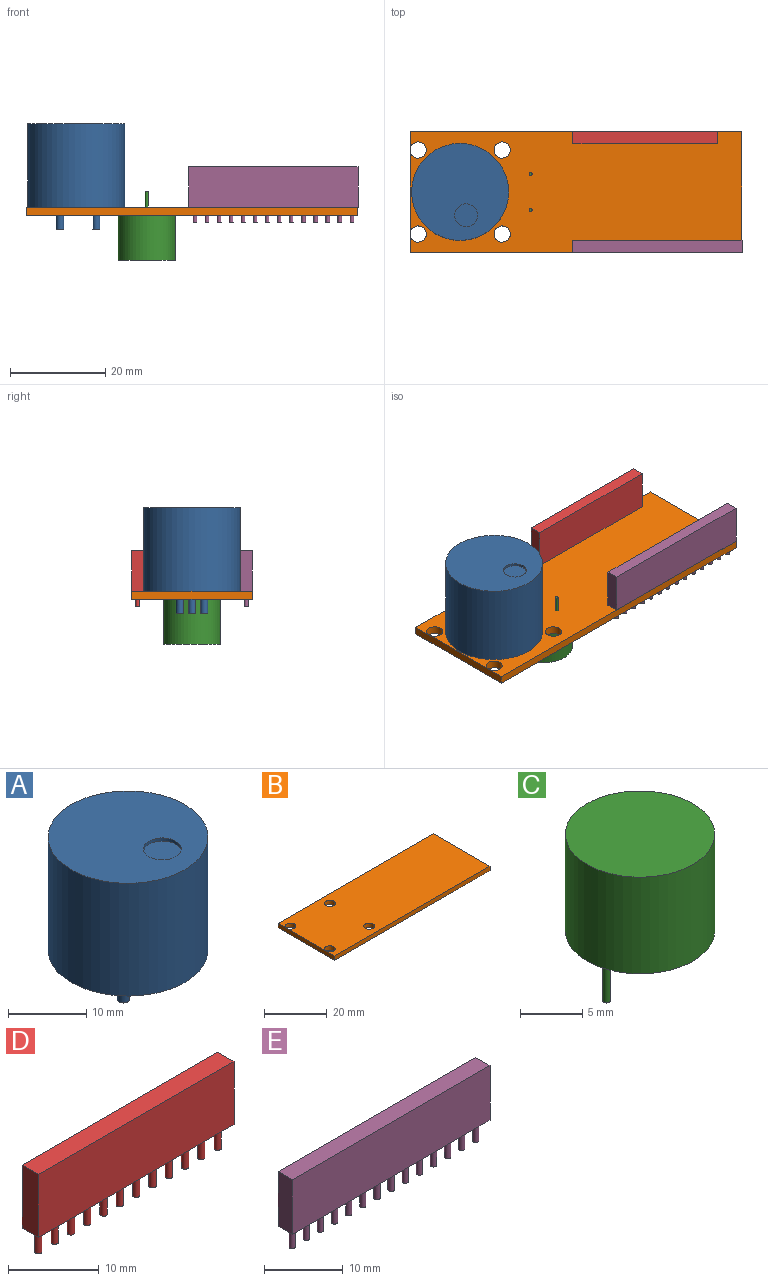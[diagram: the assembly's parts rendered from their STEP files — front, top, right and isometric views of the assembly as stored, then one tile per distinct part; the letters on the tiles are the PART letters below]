
ASSEMBLY  parts=5 mates=4
PART A: 11 faces, bbox 20.4x20.4x22.4 mm
  f0: cylinder r=10.2mm len=20.4mm, axis (0,0,-1), area 1128mm2, adj f1,f2
  f1: plane 20.4x20.4mm, normal (0,0,1), area 308.5mm2, adj f0,f9
  f2: plane 20.4x20.4mm, normal (0,0,-1), area 321mm2, adj f0,f3,f5,f7
  f3: cylinder r=0.79mm len=4.78mm, axis (0,0,1), area 23.6mm2, adj f2,f4
  f4: plane 1.57x1.57mm, normal (0,0,-1), area 1.9mm2, adj f3
  f5: cylinder r=0.79mm len=4.78mm, axis (0,0,1), area 23.6mm2, adj f2,f6
  f6: plane 1.57x1.57mm, normal (0,0,-1), area 1.9mm2, adj f5
  f7: cylinder r=0.79mm len=4.78mm, axis (0,0,1), area 23.6mm2, adj f2,f8
  f8: plane 1.57x1.57mm, normal (0,0,-1), area 1.9mm2, adj f7
  f9: cylinder r=2.42mm len=4.83mm, axis (0,0,1), area 7.6mm2, adj f1,f10
  f10: plane 4.83x4.83mm, normal (0,0,1), area 18.3mm2, adj f9
PART B: 10 faces, bbox 69.9x25.4x1.7 mm
  f0: plane 69.85x1.7mm, normal (0,1,0), area 118.7mm2, adj f1,f3,f4,f5
  f1: plane 25.4x1.7mm, normal (-1,0,0), area 43.2mm2, adj f0,f2,f4,f5
  f2: plane 69.85x1.7mm, normal (0,-1,0), area 118.7mm2, adj f1,f3,f4,f5
  f3: plane 25.4x1.7mm, normal (1,0,0), area 43.2mm2, adj f0,f2,f4,f5
  f4: plane 69.85x25.4mm, normal (0,0,-1), area 1737.9mm2, adj f0,f1,f2,f3,f6,f7,f8,f9
  f5: plane 69.85x25.4mm, normal (0,0,1), area 1737.9mm2, adj f0,f1,f2,f3,f6,f7,f8,f9
  f6: cylinder r=1.7mm len=3.4mm, axis (0,0,1), area 18.2mm2, adj f4,f5
  f7: cylinder r=1.7mm len=3.4mm, axis (0,0,1), area 18.2mm2, adj f4,f5
  f8: cylinder r=1.7mm len=3.4mm, axis (0,0,1), area 18.2mm2, adj f4,f5
  f9: cylinder r=1.7mm len=3.4mm, axis (0,0,1), area 18.2mm2, adj f4,f5
PART C: 7 faces, bbox 12x12x14.5 mm
  f0: cylinder r=6mm len=12mm, axis (0,0,-1), area 358.1mm2, adj f1,f2
  f1: plane 12x12mm, normal (0,0,1), area 113.1mm2, adj f0
  f2: plane 12x12mm, normal (0,0,-1), area 112.5mm2, adj f0,f3,f5
  f3: cylinder r=0.3mm len=5mm, axis (0,0,1), area 9.4mm2, adj f2,f4
  f4: plane 0.6x0.6mm, normal (0,0,-1), area 0.3mm2, adj f3
  f5: cylinder r=0.3mm len=5mm, axis (0,0,1), area 9.4mm2, adj f2,f6
  f6: plane 0.6x0.6mm, normal (0,0,-1), area 0.3mm2, adj f5
PART D: 30 faces, bbox 30.5x2.6x11.7 mm
  f0: plane 30.49x8.5mm, normal (0,1,0), area 259.2mm2, adj f1,f3,f4,f27
  f1: plane 8.5x2.55mm, normal (-1,0,0), area 21.7mm2, adj f0,f2,f3,f4
  f2: plane 30.49x8.5mm, normal (0,-1,0), area 259.2mm2, adj f1,f3,f4,f27
  f3: plane 30.49x2.55mm, normal (0,0,-1), area 71.7mm2, adj f0,f1,f2,f5,f7,f9,f11,f13
  f4: plane 30.49x2.55mm, normal (0,0,1), area 77.7mm2, adj f0,f1,f2,f27
  f5: cylinder r=0.4mm len=3.2mm, axis (0,0,1), area 8mm2, adj f3,f6
  f6: plane 0.8x0.8mm, normal (0,0,-1), area 0.5mm2, adj f5
  f7: cylinder r=0.4mm len=3.2mm, axis (0,0,1), area 8mm2, adj f3,f8
  f8: plane 0.8x0.8mm, normal (0,0,-1), area 0.5mm2, adj f7
  f9: cylinder r=0.4mm len=3.2mm, axis (0,0,1), area 8mm2, adj f3,f10
  f10: plane 0.8x0.8mm, normal (0,0,-1), area 0.5mm2, adj f9
  f11: cylinder r=0.4mm len=3.2mm, axis (0,0,1), area 8mm2, adj f3,f12
  f12: plane 0.8x0.8mm, normal (0,0,-1), area 0.5mm2, adj f11
  f13: cylinder r=0.4mm len=3.2mm, axis (0,0,1), area 8mm2, adj f3,f14
  f14: plane 0.8x0.8mm, normal (0,0,-1), area 0.5mm2, adj f13
  f15: cylinder r=0.4mm len=3.2mm, axis (0,0,1), area 8mm2, adj f3,f16
  f16: plane 0.8x0.8mm, normal (0,0,-1), area 0.5mm2, adj f15
  f17: cylinder r=0.4mm len=3.2mm, axis (0,0,1), area 8mm2, adj f3,f18
  f18: plane 0.8x0.8mm, normal (0,0,-1), area 0.5mm2, adj f17
  f19: cylinder r=0.4mm len=3.2mm, axis (0,0,1), area 8mm2, adj f3,f20
  f20: plane 0.8x0.8mm, normal (0,0,-1), area 0.5mm2, adj f19
  f21: cylinder r=0.4mm len=3.2mm, axis (0,0,1), area 8mm2, adj f3,f22
  f22: plane 0.8x0.8mm, normal (0,0,-1), area 0.5mm2, adj f21
  f23: cylinder r=0.4mm len=3.2mm, axis (0,0,1), area 8mm2, adj f3,f24
  f24: plane 0.8x0.8mm, normal (0,0,-1), area 0.5mm2, adj f23
  f25: cylinder r=0.4mm len=3.2mm, axis (0,0,1), area 8mm2, adj f3,f26
  f26: plane 0.8x0.8mm, normal (0,0,-1), area 0.5mm2, adj f25
  f27: plane 8.5x2.55mm, normal (1,0,0), area 21.7mm2, adj f0,f2,f3,f4
  f28: cylinder r=0.4mm len=3.2mm, axis (0,0,1), area 8mm2, adj f3,f29
  f29: plane 0.8x0.8mm, normal (0,0,-1), area 0.5mm2, adj f28
PART E: 34 faces, bbox 35.6x2.6x11.7 mm
  f0: plane 35.57x8.5mm, normal (0,1,0), area 302.3mm2, adj f1,f3,f4,f31
  f1: plane 8.5x2.55mm, normal (-1,0,0), area 21.7mm2, adj f0,f2,f3,f4
  f2: plane 35.57x8.5mm, normal (0,-1,0), area 302.3mm2, adj f1,f3,f4,f31
  f3: plane 35.57x2.55mm, normal (0,0,-1), area 83.7mm2, adj f0,f1,f2,f5,f7,f9,f11,f13
  f4: plane 35.57x2.55mm, normal (0,0,1), area 90.7mm2, adj f0,f1,f2,f31
  f5: cylinder r=0.4mm len=3.2mm, axis (0,0,1), area 8mm2, adj f3,f6
  f6: plane 0.8x0.8mm, normal (0,0,-1), area 0.5mm2, adj f5
  f7: cylinder r=0.4mm len=3.2mm, axis (0,0,1), area 8mm2, adj f3,f8
  f8: plane 0.8x0.8mm, normal (0,0,-1), area 0.5mm2, adj f7
  f9: cylinder r=0.4mm len=3.2mm, axis (0,0,1), area 8mm2, adj f3,f10
  f10: plane 0.8x0.8mm, normal (0,0,-1), area 0.5mm2, adj f9
  f11: cylinder r=0.4mm len=3.2mm, axis (0,0,1), area 8mm2, adj f3,f12
  f12: plane 0.8x0.8mm, normal (0,0,-1), area 0.5mm2, adj f11
  f13: cylinder r=0.4mm len=3.2mm, axis (0,0,1), area 8mm2, adj f3,f14
  f14: plane 0.8x0.8mm, normal (0,0,-1), area 0.5mm2, adj f13
  f15: cylinder r=0.4mm len=3.2mm, axis (0,0,1), area 8mm2, adj f3,f16
  f16: plane 0.8x0.8mm, normal (0,0,-1), area 0.5mm2, adj f15
  f17: cylinder r=0.4mm len=3.2mm, axis (0,0,1), area 8mm2, adj f3,f18
  f18: plane 0.8x0.8mm, normal (0,0,-1), area 0.5mm2, adj f17
  f19: cylinder r=0.4mm len=3.2mm, axis (0,0,1), area 8mm2, adj f3,f20
  f20: plane 0.8x0.8mm, normal (0,0,-1), area 0.5mm2, adj f19
  f21: cylinder r=0.4mm len=3.2mm, axis (0,0,1), area 8mm2, adj f3,f22
  f22: plane 0.8x0.8mm, normal (0,0,-1), area 0.5mm2, adj f21
  f23: cylinder r=0.4mm len=3.2mm, axis (0,0,1), area 8mm2, adj f3,f24
  f24: plane 0.8x0.8mm, normal (0,0,-1), area 0.5mm2, adj f23
  f25: cylinder r=0.4mm len=3.2mm, axis (0,0,1), area 8mm2, adj f3,f26
  f26: plane 0.8x0.8mm, normal (0,0,-1), area 0.5mm2, adj f25
  f27: cylinder r=0.4mm len=3.2mm, axis (0,0,1), area 8mm2, adj f3,f28
  f28: plane 0.8x0.8mm, normal (0,0,-1), area 0.5mm2, adj f27
  f29: cylinder r=0.4mm len=3.2mm, axis (0,0,1), area 8mm2, adj f3,f30
  f30: plane 0.8x0.8mm, normal (0,0,-1), area 0.5mm2, adj f29
  f31: plane 8.5x2.55mm, normal (1,0,0), area 21.7mm2, adj f0,f2,f3,f4
  f32: cylinder r=0.4mm len=3.2mm, axis (0,0,1), area 8mm2, adj f3,f33
  f33: plane 0.8x0.8mm, normal (0,0,-1), area 0.5mm2, adj f32
PLACE A t=(-25.02,0,0)mm
PLACE B at identity fixed
PLACE C rot(axis=(0.71,-0.71,0),180deg) t=(-10.16,0,-1.7)mm
PLACE D t=(0,11.43,8.5)mm
PLACE E t=(0,-11.43,8.5)mm
MATE fastened A.f2 <-> B.f5  axis (0,0,-1) through (-25,0,0)mm
MATE fastened B.f4 <-> C.f0  axis (0,0,-1) through (-10.16,0,-1.7)mm
MATE fastened B.f5 <-> D.f5  axis (0,0,1) through (0,11.43,0)mm
MATE fastened B.f5 <-> E.f5  axis (0,0,1) through (0,-11.43,0)mm
